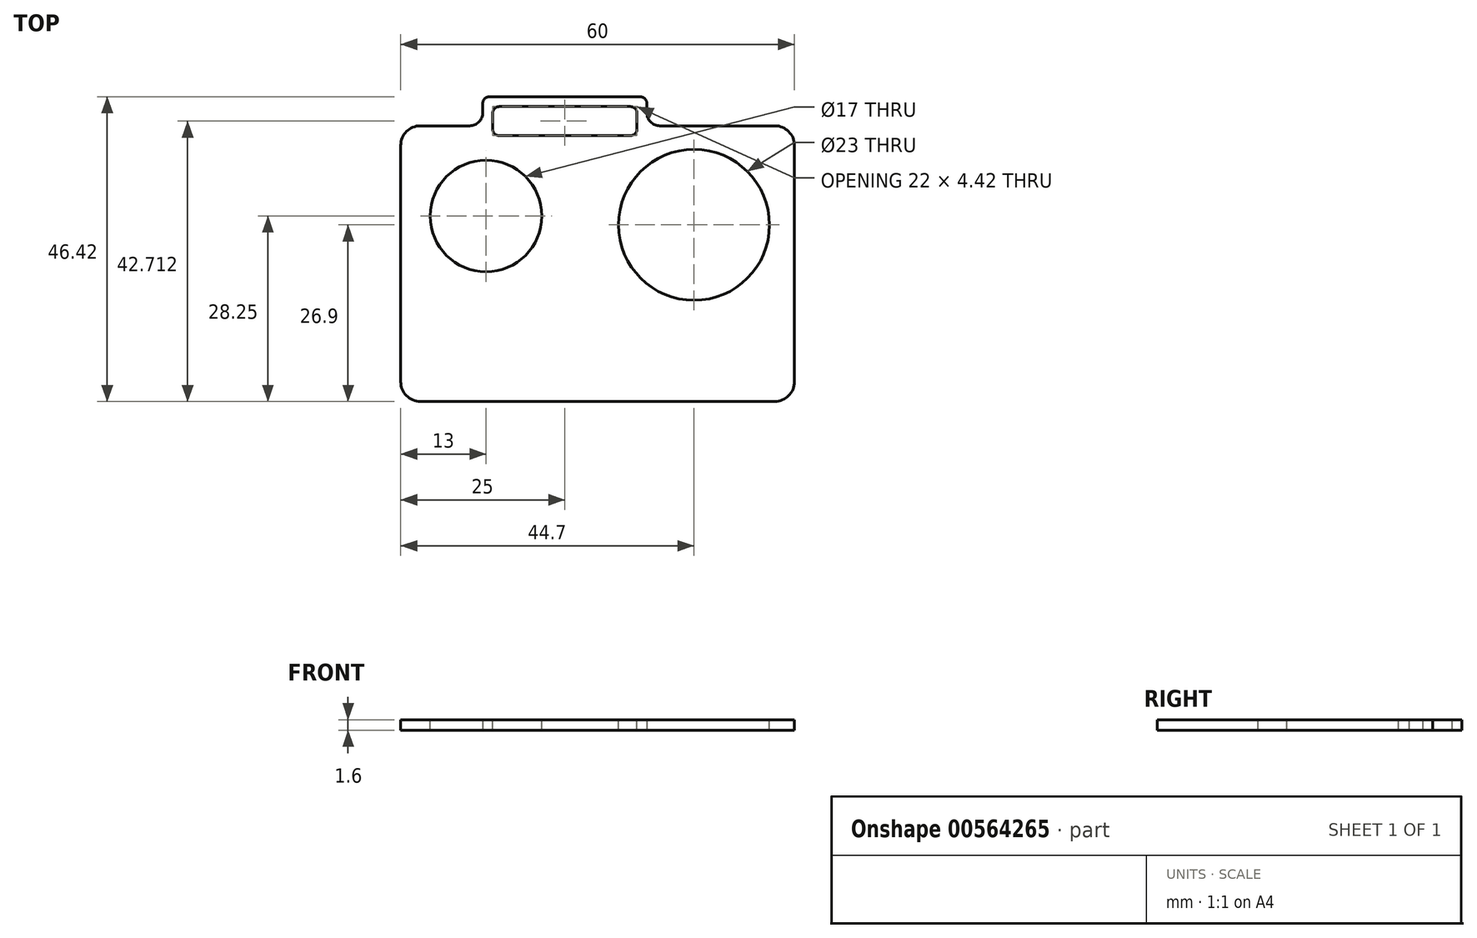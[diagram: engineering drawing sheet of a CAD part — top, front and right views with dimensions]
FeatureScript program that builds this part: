
annotation { "Feature Type Name" : "Feature", "Feature Type Description" : "" }
export const myFeature = defineFeature(function(context is Context, id is Id, definition is map)
    precondition{}
    {
        {
            var Q0;
            Q0=qCreatedBy(makeId("Top.planeOp"),FACE);
            var sketch = newSketch(context, id + "F0", { "sketchPlane" : qUnion([Q0])});
            skLineSegment(sketch, "E0.bottom", {"start": v(-30, 21) * mm, "end": v(30, 21) * mm});
            skLineSegment(sketch, "E0.top", {"start": v(-30, -21) * mm, "end": v(30, -21) * mm});
            skLineSegment(sketch, "E0.left", {"start": v(-30, 21) * mm, "end": v(-30, -21) * mm});
            skLineSegment(sketch, "E0.right", {"start": v(30, 21) * mm, "end": v(30, -21) * mm});
            skSolve(sketch);
        }
        {
            var Q0;
            Q0 = qSketchRegion(id + "F0", true);
            extrude(context, id + "F1", {"entities" : qUnion([Q0]), "depth" : 1.6 * mm, "offsetDistance" : 25 * mm});
        }
        {
            var Q0;
            Q0=makeQuery(id+"F1.opExtrude","CAP_FACE",FACE,{"disambiguationData":[OSD([sQuery(id+"F0.wireOp",EDGE,"E0.bottom"),sQuery(id+"F0.wireOp",EDGE,"E0.top"),sQuery(id+"F0.wireOp",EDGE,"E0.left"),sQuery(id+"F0.wireOp",EDGE,"E0.right")])],"isStart":false});
            var sketch = newSketch(context, id + "F2", { "sketchPlane" : qUnion([Q0])});
            skCircle(sketch, "E1", {"center": v(14.7, 5.9) * mm, "radius": 11.5 * mm});
            skCircle(sketch, "E2", {"center": v(-17, 7.25) * mm, "radius": 8.5 * mm});
            skSolve(sketch);
        }
        {
            var Q0;
            Q0 = qSketchRegion(id + "F2", true);
            extrude(context, id + "F3", {"entities" : qUnion([Q0]), "operationType" : NewBodyOperationType.REMOVE, "endBound" : BoundingType.THROUGH_ALL, "oppositeDirection" : true, "depth" : 25 * mm, "offsetDistance" : 25 * mm});
        }
        {
            var Q0;
            Q0=qCreatedBy(makeId("Top.planeOp"),FACE);
            var sketch = newSketch(context, id + "F4", { "sketchPlane" : qUnion([Q0])});
            skLineSegment(sketch, "E3.bottom", {"start": v(-17.5, 20.92) * mm, "end": v(-16, 20.92) * mm});
            skLineSegment(sketch, "E3.top", {"start": v(-17.5, 25.42) * mm, "end": v(7.5, 25.42) * mm});
            skLineSegment(sketch, "E3.left", {"start": v(-17.5, 20.92) * mm, "end": v(-17.5, 25.42) * mm});
            skLineSegment(sketch, "E3.right", {"start": v(7.5, 20.92) * mm, "end": v(7.5, 25.42) * mm});
            skLineSegment(sketch, "E4.top", {"start": v(-16, 23.92) * mm, "end": v(6, 23.92) * mm});
            skLineSegment(sketch, "E4.left", {"start": v(-16, 20.92) * mm, "end": v(-16, 23.92) * mm});
            skLineSegment(sketch, "E4.right", {"start": v(6, 20.92) * mm, "end": v(6, 23.92) * mm});
            skLineSegment(sketch, "E5.trimOffspring", {"start": v(6, 20.92) * mm, "end": v(7.5, 20.92) * mm});
            skSolve(sketch);
        }
        {
            var Q0;
            Q0 = qSketchRegion(id + "F4", true);
            extrude(context, id + "F5", {"entities" : qUnion([Q0]), "operationType" : NewBodyOperationType.ADD, "depth" : 1.6 * mm, "offsetDistance" : 25 * mm});
        }
        {
            var Q0;
            Q0=makeQuery(id+"F1.opExtrude","SWEPT_EDGE",EDGE,{"disambiguationData":[OSD([sQuery(id+"F0.wireOp",EDGE,"E0.bottom"),sQuery(id+"F0.wireOp",EDGE,"E0.left")])]});
            var Q1;
            Q1=makeQuery(id+"F1.opExtrude","SWEPT_EDGE",EDGE,{"disambiguationData":[OSD([sQuery(id+"F0.wireOp",EDGE,"E0.top"),sQuery(id+"F0.wireOp",EDGE,"E0.left")])]});
            var Q2;
            Q2=makeQuery(id+"F1.opExtrude","SWEPT_EDGE",EDGE,{"disambiguationData":[OSD([sQuery(id+"F0.wireOp",EDGE,"E0.bottom"),sQuery(id+"F0.wireOp",EDGE,"E0.right")])]});
            var Q3;
            Q3=makeQuery(id+"F1.opExtrude","SWEPT_EDGE",EDGE,{"disambiguationData":[OSD([sQuery(id+"F0.wireOp",EDGE,"E0.top"),sQuery(id+"F0.wireOp",EDGE,"E0.right")])]});
            fillet(context, id + "F6", {"entities" : qUnion([Q0, Q1, Q2, Q3]), "radius" : 3 * mm, "tangentPropagation" : true, "allowEdgeOverflow" : false});
        }
        {
            var Q0;
            Q0=makeQuery(id+"F5.boolean.opBoolean","INTERSECT",EDGE,{"derivedFrom":[makeQuery(id+"F1.opExtrude","SWEPT_FACE",FACE,{"disambiguationData":[OSD([sQuery(id+"F0.wireOp",EDGE,"E0.bottom")])]}),makeQuery(id+"F5.opExtrude","SWEPT_FACE",FACE,{"disambiguationData":[OSD([sQuery(id+"F4.wireOp",EDGE,"E3.left")])]})]});
            var Q1;
            Q1=makeQuery(id+"F5.boolean.opBoolean","INTERSECT",EDGE,{"derivedFrom":[makeQuery(id+"F1.opExtrude","SWEPT_FACE",FACE,{"disambiguationData":[OSD([sQuery(id+"F0.wireOp",EDGE,"E0.bottom")])]}),makeQuery(id+"F5.opExtrude","SWEPT_FACE",FACE,{"disambiguationData":[OSD([sQuery(id+"F4.wireOp",EDGE,"E3.right")])]})]});
            fillet(context, id + "F7", {"entities" : qUnion([Q0, Q1]), "radius" : 2 * mm, "tangentPropagation" : true, "allowEdgeOverflow" : false});
        }
        {
            var Q0;
            Q0=makeQuery(id+"F5.boolean.opBoolean","MERGE",FACE,{"derivedFrom":[makeQuery(id+"F1.opExtrude","CAP_FACE",FACE,{"disambiguationData":[OSD([sQuery(id+"F0.wireOp",EDGE,"E0.bottom"),sQuery(id+"F0.wireOp",EDGE,"E0.top"),sQuery(id+"F0.wireOp",EDGE,"E0.left"),sQuery(id+"F0.wireOp",EDGE,"E0.right")])],"isStart":false}),makeQuery(id+"F5.opExtrude","CAP_FACE",FACE,{"disambiguationData":[OSD([sQuery(id+"F4.wireOp",EDGE,"E3.bottom"),sQuery(id+"F4.wireOp",EDGE,"E3.top"),sQuery(id+"F4.wireOp",EDGE,"E3.left"),sQuery(id+"F4.wireOp",EDGE,"E3.right"),sQuery(id+"F4.wireOp",EDGE,"E4.top"),sQuery(id+"F4.wireOp",EDGE,"E4.left"),sQuery(id+"F4.wireOp",EDGE,"E4.right"),sQuery(id+"F4.wireOp",EDGE,"E5.trimOffspring")])],"isStart":false})]});
            var sketch = newSketch(context, id + "F8", { "sketchPlane" : qUnion([Q0])});
            skLineSegment(sketch, "E6.bottom", {"start": v(-16, 21) * mm, "end": v(6, 21) * mm});
            skLineSegment(sketch, "E6.top", {"start": v(-16, 19.5) * mm, "end": v(6, 19.5) * mm});
            skLineSegment(sketch, "E6.left", {"start": v(-16, 21) * mm, "end": v(-16, 19.5) * mm});
            skLineSegment(sketch, "E6.right", {"start": v(6, 21) * mm, "end": v(6, 19.5) * mm});
            skSolve(sketch);
        }
        {
            var Q0;
            Q0 = qSketchRegion(id + "F8", true);
            extrude(context, id + "F9", {"entities" : qUnion([Q0]), "operationType" : NewBodyOperationType.REMOVE, "endBound" : BoundingType.THROUGH_ALL, "oppositeDirection" : true, "depth" : 25 * mm, "offsetDistance" : 25 * mm});
        }
        {
            var Q0;
            Q0=makeQuery(id+"F5.opExtrude","SWEPT_EDGE",EDGE,{"disambiguationData":[OSD([sQuery(id+"F4.wireOp",EDGE,"E4.top"),sQuery(id+"F4.wireOp",EDGE,"E4.left")])]});
            var Q1;
            Q1=makeQuery(id+"F5.opExtrude","SWEPT_EDGE",EDGE,{"disambiguationData":[OSD([sQuery(id+"F4.wireOp",EDGE,"E4.top"),sQuery(id+"F4.wireOp",EDGE,"E4.right")])]});
            var Q2;
            Q2=makeQuery(id+"F5.opExtrude","SWEPT_EDGE",EDGE,{"disambiguationData":[OSD([sQuery(id+"F4.wireOp",EDGE,"E3.top"),sQuery(id+"F4.wireOp",EDGE,"E3.right")])]});
            var Q3;
            Q3=makeQuery(id+"F5.opExtrude","SWEPT_EDGE",EDGE,{"disambiguationData":[OSD([sQuery(id+"F4.wireOp",EDGE,"E3.top"),sQuery(id+"F4.wireOp",EDGE,"E3.left")])]});
            var Q4;
            Q4=makeQuery(id+"F9.boolean.opBoolean","COPY",EDGE,{"derivedFrom":makeQuery(id+"F9.opExtrude","SWEPT_EDGE",EDGE,{"disambiguationData":[OSD([sQuery(id+"F8.wireOp",EDGE,"E6.top"),sQuery(id+"F8.wireOp",EDGE,"E6.left")])]})});
            var Q5;
            Q5=makeQuery(id+"F9.boolean.opBoolean","COPY",EDGE,{"derivedFrom":makeQuery(id+"F9.opExtrude","SWEPT_EDGE",EDGE,{"disambiguationData":[OSD([sQuery(id+"F8.wireOp",EDGE,"E6.top"),sQuery(id+"F8.wireOp",EDGE,"E6.right")])]})});
            fillet(context, id + "F10", {"entities" : qUnion([Q0, Q1, Q2, Q3, Q4, Q5]), "radius" : 1 * mm, "tangentPropagation" : true, "allowEdgeOverflow" : false});
        }
    });
